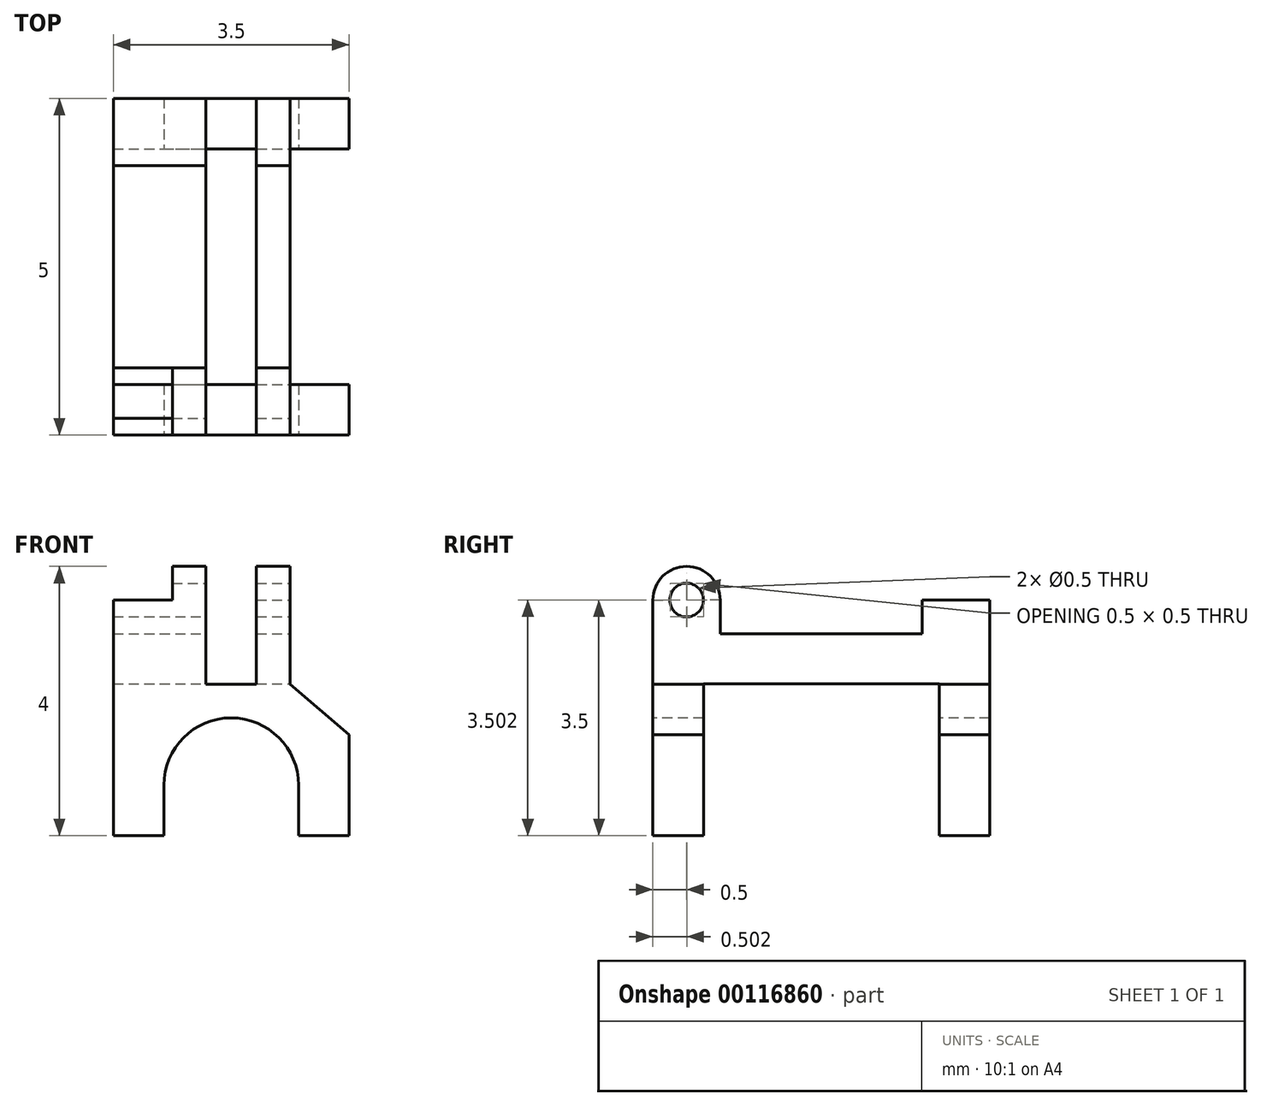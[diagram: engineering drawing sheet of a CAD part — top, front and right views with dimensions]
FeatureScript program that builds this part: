
annotation { "Feature Type Name" : "Feature", "Feature Type Description" : "" }
export const myFeature = defineFeature(function(context is Context, id is Id, definition is map)
    precondition{}
    {
        {
            var Q0;
            Q0=qCreatedBy(makeId("Right.planeOp"),FACE);
            var sketch = newSketch(context, id + "F0", { "sketchPlane" : qUnion([Q0])});
            skLineSegment(sketch, "E0.bottom", {"start": v(-2.5, 1.75) * mm, "end": v(2.5, 1.75) * mm});
            skLineSegment(sketch, "E0.top", {"start": v(-2.5, -1.75) * mm, "end": v(2.5, -1.75) * mm});
            skLineSegment(sketch, "E0.left", {"start": v(-2.5, 1.75) * mm, "end": v(-2.5, -1.75) * mm});
            skLineSegment(sketch, "E0.right", {"start": v(2.5, 1.75) * mm, "end": v(2.5, -1.75) * mm});
            skSolve(sketch);
        }
        {
            var Q0;
            Q0 = qSketchRegion(id + "F0", true);
            var Q1;
            Q1=makeQuery(id+"F0.imprint","IMPRINT",FACE,{"disambiguationData":[TD([[makeQuery(id+"F0.imprint","IMPRINT",EDGE,{"derivedFrom":sQuery(id+"F0.wireOp",EDGE,"E0.bottom")}),-1.0]])]});
            extrude(context, id + "F1", {"entities" : qUnion([Q0, Q1]), "endBound" : BoundingType.SYMMETRIC, "depth" : 3.5 * mm});
        }
        {
            var Q0;
            Q0=makeQuery(id+"F1.opExtrude","SWEPT_FACE",FACE,{"disambiguationData":[OSD([sQuery(id+"F0.wireOp",EDGE,"E0.left")])]});
            var sketch = newSketch(context, id + "F2", { "sketchPlane" : qUnion([Q0])});
            skLineSegment(sketch, "E1", {"start": v(1.75, -1.75) * mm, "end": v(1.75, -0.25) * mm});
            skPoint(sketch, "E2.endSnap0", {"position": v(0, -1.75) * mm});
            skLineSegment(sketch, "E3", {"start": v(1.75, -1.75) * mm, "end": v(1, -1.75) * mm});
            skLineSegment(sketch, "E4.MirrorCS", {"start": v(-1.75, -1.75) * mm, "end": v(-1, -1.75) * mm});
            skArc(sketch, "E5", {"start": v(1, -1) * mm, "mid": v(0, 0) * mm, "end": v(-1, -1) * mm});
            skLineSegment(sketch, "E6", {"start": v(-1, -1.75) * mm, "end": v(-1, -1) * mm});
            skLineSegment(sketch, "E7", {"start": v(1, -1.75) * mm, "end": v(1, -1) * mm});
            skLineSegment(sketch, "E8.MirrorCS", {"start": v(-1.75, -1.75) * mm, "end": v(-1.75, -0.25) * mm});
            skPoint(sketch, "E9.endSnap0", {"position": v(0, 1.75) * mm});
            skLineSegment(sketch, "E10", {"start": v(0, 0.5) * mm, "end": v(-0.37, 0.5) * mm});
            skLineSegment(sketch, "E11.MirrorCS", {"start": v(0, 0.5) * mm, "end": v(0.38, 0.5) * mm});
            skLineSegment(sketch, "E12", {"start": v(-1.75, -0.25) * mm, "end": v(-0.87, 0.5) * mm});
            skLineSegment(sketch, "E13", {"start": v(0.87, 0.5) * mm, "end": v(1.75, -0.25) * mm});
            skLineSegment(sketch, "E14", {"start": v(-0.87, 0.5) * mm, "end": v(-0.87, 1.75) * mm});
            skLineSegment(sketch, "E15", {"start": v(0.87, 0.5) * mm, "end": v(0.87, 1.75) * mm});
            skLineSegment(sketch, "E16", {"start": v(-0.87, 1.75) * mm, "end": v(0.87, 1.75) * mm});
            skLineSegment(sketch, "E17", {"start": v(-0.38, 1.75) * mm, "end": v(-0.37, 0.5) * mm});
            skLineSegment(sketch, "E18", {"start": v(0.37, 1.75) * mm, "end": v(0.38, 0.5) * mm});
            skLineSegment(sketch, "E19", {"start": v(-0.38, 1.75) * mm, "end": v(-0.87, 1.75) * mm});
            skLineSegment(sketch, "E20", {"start": v(0.37, 1.75) * mm, "end": v(0.87, 1.75) * mm});
            skSolve(sketch);
        }
        {
            var Q0;
            {var subQ0=sQuery(id+"F2.wireOp",EDGE,"E12");Q0=makeQuery(id+"F2.imprint","IMPRINT",FACE,{"disambiguationData":[TD([[makeQuery(id+"F2.imprint","IMPRINT",EDGE,{"derivedFrom":subQ0}),1.0]])]});}
            var sketch = newSketch(context, id + "F3", { "sketchPlane" : qUnion([Q0])});
            skSolve(sketch);
        }
        {
            var Q0;
            {var subQ0=sQuery(id+"F2.wireOp",EDGE,"E13");Q0=makeQuery(id+"F2.imprint","IMPRINT",FACE,{"disambiguationData":[TD([[makeQuery(id+"F2.imprint","IMPRINT",EDGE,{"derivedFrom":subQ0}),1.0]])]});}
            var Q1;
            Q1=makeQuery(id+"F2.imprint","IMPRINT",FACE,{"disambiguationData":[TD([[makeQuery(id+"F2.imprint","IMPRINT",EDGE,{"derivedFrom":sQuery(id+"F2.wireOp",EDGE,"E5")}),1.0]])]});
            var Q2;
            {var subQ0=sQuery(id+"F2.wireOp",EDGE,"E12");Q2=makeQuery(id+"F3.imprint","IMPRINT",FACE,{"disambiguationData":[TD([[makeQuery(id+"F3.imprint","IMPRINT",EDGE,{"derivedFrom":makeQuery(id+"F2.imprint","IMPRINT",EDGE,{"derivedFrom":subQ0})}),1.0]])]});}
            var Q3;
            Q3=makeQuery(id+"F2.imprint","IMPRINT",FACE,{"disambiguationData":[TD([[makeQuery(id+"F2.imprint","IMPRINT",EDGE,{"derivedFrom":sQuery(id+"F2.wireOp",EDGE,"E10")}),-1.0]])]});
            extrude(context, id + "F4", {"entities" : qUnion([Q0, Q1, Q2, Q3]), "operationType" : NewBodyOperationType.REMOVE, "oppositeDirection" : true, "depth" : 25 * mm});
        }
        {
            var Q0;
            Q0=makeQuery(id+"F1.opExtrude","CAP_FACE",FACE,{"disambiguationData":[OSD([sQuery(id+"F0.wireOp",EDGE,"E0.bottom"),sQuery(id+"F0.wireOp",EDGE,"E0.top"),sQuery(id+"F0.wireOp",EDGE,"E0.left"),sQuery(id+"F0.wireOp",EDGE,"E0.right")])],"isStart":false});
            var sketch = newSketch(context, id + "F5", { "sketchPlane" : qUnion([Q0])});
            skLineSegment(sketch, "E21", {"start": v(-1.75, -0.25) * mm, "end": v(-1.75, -1.75) * mm});
            skLineSegment(sketch, "E22", {"start": v(-1.75, -0.25) * mm, "end": v(-1.75, 0.5) * mm});
            skLineSegment(sketch, "E23.MirrorCS", {"start": v(1.75, -0.25) * mm, "end": v(1.75, 0.5) * mm});
            skLineSegment(sketch, "E24.MirrorCS", {"start": v(1.75, -0.25) * mm, "end": v(1.75, -1.75) * mm});
            skLineSegment(sketch, "E25", {"start": v(-1.75, 0.5) * mm, "end": v(1.75, 0.5) * mm});
            skLineSegment(sketch, "E26", {"start": v(-1.75, -0.25) * mm, "end": v(1.75, -0.25) * mm});
            skSolve(sketch);
        }
        {
            var Q0;
            Q0 = qSketchRegion(id + "F5", true);
            var Q1;
            {var subQ0=sQuery(id+"F5.wireOp",EDGE,"E21");Q1=makeQuery(id+"F5.imprint","IMPRINT",FACE,{"disambiguationData":[TD([[makeQuery(id+"F5.imprint","IMPRINT",EDGE,{"derivedFrom":subQ0}),1.0]])]});}
            extrude(context, id + "F6", {"entities" : qUnion([Q0, Q1]), "operationType" : NewBodyOperationType.REMOVE, "oppositeDirection" : true, "depth" : 25 * mm});
        }
        {
            var Q0;
            Q0=makeQuery(id+"F4.boolean.opBoolean","COPY",FACE,{"derivedFrom":makeQuery(id+"F4.opExtrude","SWEPT_FACE",FACE,{"disambiguationData":[OSD([sQuery(id+"F2.wireOp",EDGE,"E15")])]})});
            var sketch = newSketch(context, id + "F7", { "sketchPlane" : qUnion([Q0])});
            skLineSegment(sketch, "E27", {"start": v(2.5, 1.75) * mm, "end": v(1.5, 1.75) * mm});
            skLineSegment(sketch, "E28", {"start": v(1.5, 1.75) * mm, "end": v(1.5, 1.25) * mm});
            skLineSegment(sketch, "E29", {"start": v(-1.5, 1.75) * mm, "end": v(-1.5, 1.25) * mm});
            skLineSegment(sketch, "E30", {"start": v(-1.5, 1.25) * mm, "end": v(1.5, 1.25) * mm});
            skSolve(sketch);
        }
        {
            var Q0;
            {var subQ0=sQuery(id+"F7.wireOp",EDGE,"E28");Q0=makeQuery(id+"F7.imprint","IMPRINT",FACE,{"disambiguationData":[TD([[makeQuery(id+"F7.imprint","IMPRINT",EDGE,{"derivedFrom":subQ0}),-1.0]])]});}
            extrude(context, id + "F8", {"entities" : qUnion([Q0]), "operationType" : NewBodyOperationType.REMOVE, "oppositeDirection" : true, "depth" : 25 * mm});
        }
        {
            var Q0;
            Q0=makeQuery(id+"F4.boolean.opBoolean","COPY",FACE,{"derivedFrom":makeQuery(id+"F4.opExtrude","SWEPT_FACE",FACE,{"disambiguationData":[OSD([sQuery(id+"F2.wireOp",EDGE,"E15")])]})});
            var sketch = newSketch(context, id + "F9", { "sketchPlane" : qUnion([Q0])});
            skCircle(sketch, "E31", {"center": v(-2, 1.75) * mm, "radius": 0.25 * mm});
            skSolve(sketch);
        }
        {
            var Q0;
            {var subQ0=sQuery(id+"F9.wireOp",EDGE,"E31");var subQ1=sQuery(id+"F0.wireOp",EDGE,"E0.bottom");var subQ2=sQuery(id+"F0.wireOp",EDGE,"E0.left");var subQ3=sQuery(id+"F2.wireOp",EDGE,"E15");var subQ4=makeQuery(id+"F8.boolean.opBoolean","SPLIT",EDGE,{"disambiguationData":[TD([makeQuery(id+"F1.opExtrude","SWEPT_FACE",FACE,{"disambiguationData":[OSD([subQ2])]})])],"derivedFrom":makeQuery(id+"F4.boolean.opBoolean","COPY",EDGE,{"derivedFrom":makeQuery(id+"F4.opExtrude","SWEPT_EDGE",EDGE,{"disambiguationData":[OSD([subQ1,subQ2,subQ3,sQuery(id+"F2.wireOp",EDGE,"E20")])]})})});var subQ5=makeQuery(id+"F9.imprint","INTERSECT",VERTEX,{"disambiguationData":[OD(0.0)],"derivedFrom":[subQ4,subQ0]});Q0=makeQuery(id+"F9.imprint","IMPRINT",FACE,{"disambiguationData":[TD([[makeQuery(id+"F9.imprint","IMPRINT",EDGE,{"disambiguationData":[TD([[subQ5,-1.0]])],"derivedFrom":subQ0}),1.0]])]});}
            extrude(context, id + "F10", {"entities" : qUnion([Q0]), "operationType" : NewBodyOperationType.REMOVE, "oppositeDirection" : true, "depth" : 25 * mm});
        }
        {
            var Q0;
            Q0=makeQuery(id+"F4.boolean.opBoolean","COPY",FACE,{"derivedFrom":makeQuery(id+"F4.opExtrude","SWEPT_FACE",FACE,{"disambiguationData":[OSD([sQuery(id+"F2.wireOp",EDGE,"E15")])]})});
            var sketch = newSketch(context, id + "F11", { "sketchPlane" : qUnion([Q0])});
            skArc(sketch, "E32", {"start": v(-1.5, 1.75) * mm, "mid": v(-2, 2.25) * mm, "end": v(-2.5, 1.75) * mm});
            skLineSegment(sketch, "E33", {"start": v(-1.5, 1.75) * mm, "end": v(-1.5, 1.25) * mm});
            skLineSegment(sketch, "E34", {"start": v(-2.5, 1.75) * mm, "end": v(-2.5, 0.5) * mm});
            skCircle(sketch, "E35", {"center": v(-2, 1.75) * mm, "radius": 0.25 * mm});
            skSolve(sketch);
        }
        {
            var Q0;
            Q0=makeQuery(id+"F11.imprint","IMPRINT",FACE,{"disambiguationData":[TD([[makeQuery(id+"F11.imprint","IMPRINT",EDGE,{"derivedFrom":sQuery(id+"F11.wireOp",EDGE,"E32")}),1.0]])]});
            extrude(context, id + "F12", {"entities" : qUnion([Q0]), "operationType" : NewBodyOperationType.ADD, "oppositeDirection" : true, "depth" : 1.75 * mm});
        }
        {
            var Q0;
            Q0=makeQuery(id+"F1.opExtrude","SWEPT_FACE",FACE,{"disambiguationData":[OSD([sQuery(id+"F0.wireOp",EDGE,"E0.left")])]});
            var sketch = newSketch(context, id + "F13", { "sketchPlane" : qUnion([Q0])});
            skLineSegment(sketch, "E36", {"start": v(-0.38, 0.5) * mm, "end": v(-0.38, 2.4) * mm});
            skPoint(sketch, "E36.endSnap0", {"position": v(-0.38, 1.12) * mm});
            skLineSegment(sketch, "E37", {"start": v(-0.38, 2.4) * mm, "end": v(0.38, 2.4) * mm});
            skLineSegment(sketch, "E38", {"start": v(0.38, 2.4) * mm, "end": v(0.38, 0.5) * mm});
            skLineSegment(sketch, "E39", {"start": v(0.38, 0.5) * mm, "end": v(-0.38, 0.5) * mm});
            skSolve(sketch);
        }
        {
            var Q0;
            Q0 = qSketchRegion(id + "F13", true);
            var Q1;
            {var subQ9=sQuery(id+"F13.wireOp",EDGE,"E37");Q1=makeQuery(id+"F13.imprint","IMPRINT",FACE,{"disambiguationData":[TD([[makeQuery(id+"F13.imprint","IMPRINT",EDGE,{"derivedFrom":subQ9}),-1.0]])]});}
            extrude(context, id + "F14", {"entities" : qUnion([Q0, Q1]), "operationType" : NewBodyOperationType.REMOVE, "oppositeDirection" : true, "depth" : 25 * mm});
        }
    });
